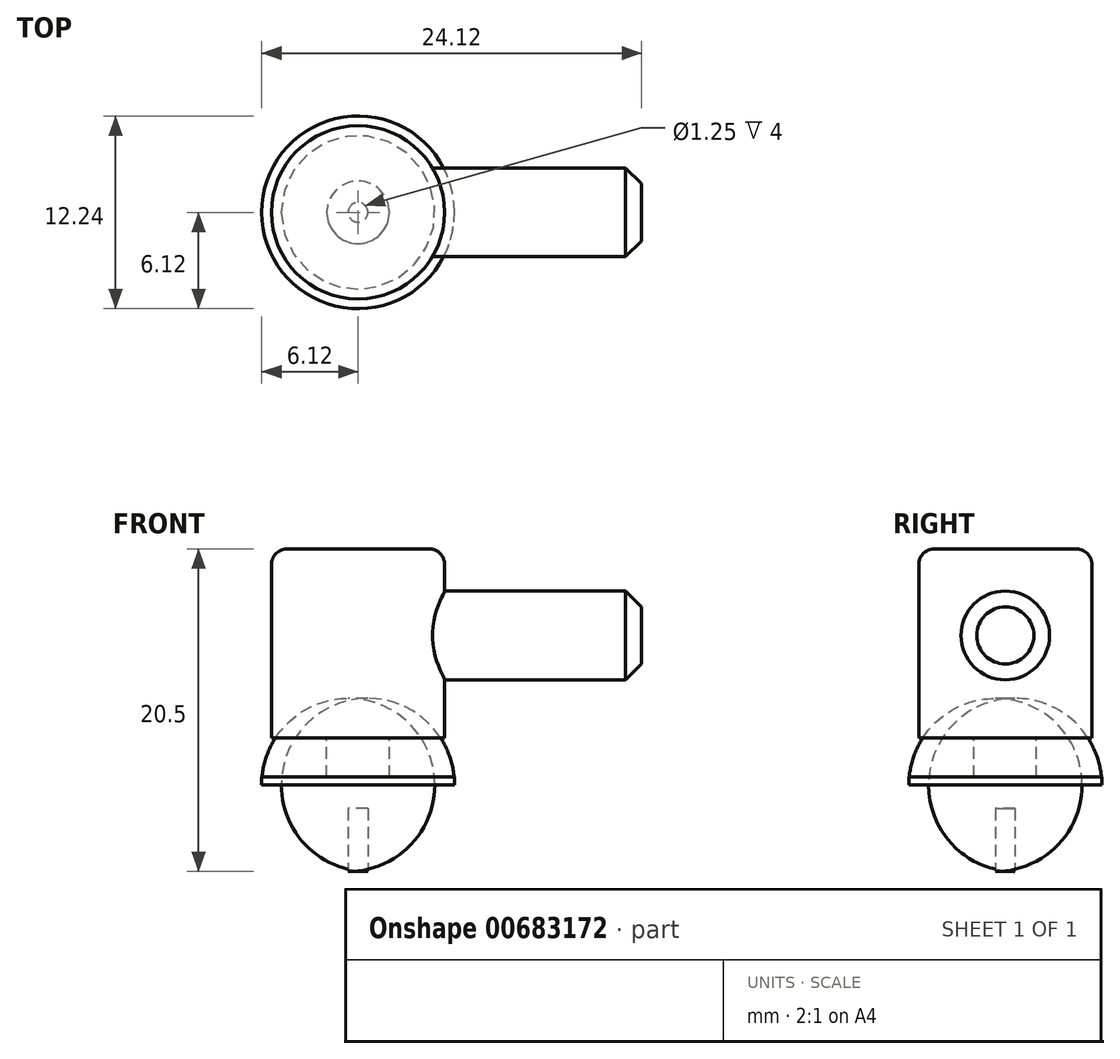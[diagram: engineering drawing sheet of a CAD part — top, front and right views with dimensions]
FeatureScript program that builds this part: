
annotation { "Feature Type Name" : "Feature", "Feature Type Description" : "" }
export const myFeature = defineFeature(function(context is Context, id is Id, definition is map)
    precondition{}
    {
        {
            var Q0;
            Q0=qCreatedBy(makeId("Top.planeOp"),FACE);
            var sketch = newSketch(context, id + "F0", { "sketchPlane" : qUnion([Q0])});
            skCircle(sketch, "E0", {"center": v(0, 0) * mm, "radius": 5.5 * mm});
            skSolve(sketch);
        }
        {
            var Q0;
            Q0=makeQuery(id+"F0.imprint","IMPRINT",FACE,{"disambiguationData":[TD([[makeQuery(id+"F0.imprint","IMPRINT",EDGE,{"derivedFrom":sQuery(id+"F0.wireOp",EDGE,"E0")}),1.0]])]});
            extrude(context, id + "F1", {"entities" : qUnion([Q0]), "depth" : 12 * mm, "offsetDistance" : 25 * mm});
        }
        {
            var Q0;
            Q0=makeQuery(id+"F1.opExtrude","CAP_EDGE",EDGE,{"disambiguationData":[OSD([sQuery(id+"F0.wireOp",EDGE,"E0")])],"isStart":false});
            fillet(context, id + "F2", {"entities" : qUnion([Q0]), "radius" : 1 * mm, "tangentPropagation" : true, "allowEdgeOverflow" : false});
        }
        {
            var Q0;
            Q0=makeQuery(id+"F1.opExtrude","CAP_FACE",FACE,{"disambiguationData":[OSD([sQuery(id+"F0.wireOp",EDGE,"E0")])],"isStart":true});
            var sketch = newSketch(context, id + "F3", { "sketchPlane" : qUnion([Q0])});
            skCircle(sketch, "E1", {"center": v(0, 0) * mm, "radius": 1.99 * mm});
            skSolve(sketch);
        }
        {
            var Q0;
            Q0=makeQuery(id+"F3.imprint","IMPRINT",FACE,{"disambiguationData":[TD([[makeQuery(id+"F3.imprint","IMPRINT",EDGE,{"derivedFrom":sQuery(id+"F3.wireOp",EDGE,"E1")}),1.0]])]});
            extrude(context, id + "F4", {"entities" : qUnion([Q0]), "operationType" : NewBodyOperationType.ADD, "depth" : 5 * mm, "offsetDistance" : 25 * mm});
        }
        {
            var Q0;
            Q0=qCreatedBy(makeId("Top.planeOp"),FACE);
            cPlane(context, id + "F5", {"entities" : qUnion([Q0]), "cplaneType" : CPlaneType.OFFSET, "offset" : 2.5 * mm, "oppositeDirection" : true, "width" : 150 * mm, "height" : 150 * mm});
        }
        {
            var Q0;
            Q0=qCreatedBy(id+"F5.planeOp",FACE);
            var sketch = newSketch(context, id + "F6", { "sketchPlane" : qUnion([Q0])});
            skCircle(sketch, "E2", {"center": v(0, 0) * mm, "radius": 6.12 * mm});
            skSolve(sketch);
        }
        {
            var Q0;
            Q0=makeQuery(id+"F6.imprint","IMPRINT",FACE,{"disambiguationData":[TD([[makeQuery(id+"F6.imprint","IMPRINT",EDGE,{"derivedFrom":sQuery(id+"F6.wireOp",EDGE,"E2")}),1.0]])]});
            extrude(context, id + "F7", {"entities" : qUnion([Q0]), "operationType" : NewBodyOperationType.ADD, "oppositeDirection" : true, "depth" : 6 * mm, "offsetDistance" : 25 * mm});
        }
        {
            var Q0;
            Q0=makeQuery(id+"F7.opExtrude","CAP_EDGE",EDGE,{"disambiguationData":[OSD([sQuery(id+"F6.wireOp",EDGE,"E2")])],"isStart":false});
            fillet(context, id + "F8", {"entities" : qUnion([Q0]), "radius" : 5.5 * mm, "tangentPropagation" : true, "allowEdgeOverflow" : false});
        }
        {
            var Q0;
            Q0=makeQuery(id+"F7.opExtrude","CAP_FACE",FACE,{"disambiguationData":[OSD([sQuery(id+"F6.wireOp",EDGE,"E2")])],"isStart":false});
            var Q1;
            Q1=sQuery(id+"FbIusUFVjKy5Sbp_1.wireOp",EDGE,"gtMB0ZUI-0d9O-3fgz-Bf66-AF4htYF9QBhT");
            extrude(context, id + "F9", {"entities" : qUnion([Q0]), "operationType" : NewBodyOperationType.REMOVE, "surfaceEntities" : qUnion([Q1]), "oppositeDirection" : true, "depth" : 4 * mm, "offsetDistance" : 25 * mm});
        }
        {
            var Q0;
            Q0=qCreatedBy(makeId("Right.planeOp"),FACE);
            var sketch = newSketch(context, id + "F10", { "sketchPlane" : qUnion([Q0])});
            skCircle(sketch, "E3", {"center": v(0, 6.5) * mm, "radius": 2.81 * mm});
            skSolve(sketch);
        }
        {
            var Q0;
            Q0=qSketchRegion(id+"F10",true);
            extrude(context, id + "F11", {"entities" : qUnion([Q0]), "operationType" : NewBodyOperationType.ADD, "depth" : 18 * mm, "offsetDistance" : 25 * mm});
        }
        {
            var Q0;
            Q0=makeQuery(id+"F11.opExtrude","CAP_EDGE",EDGE,{"disambiguationData":[OSD([sQuery(id+"F10.wireOp",EDGE,"E3")])],"isStart":false});
            chamfer(context, id + "F12", {"entities" : qUnion([Q0]), "width" : 1 * mm, "tangentPropagation" : true});
        }
    });
